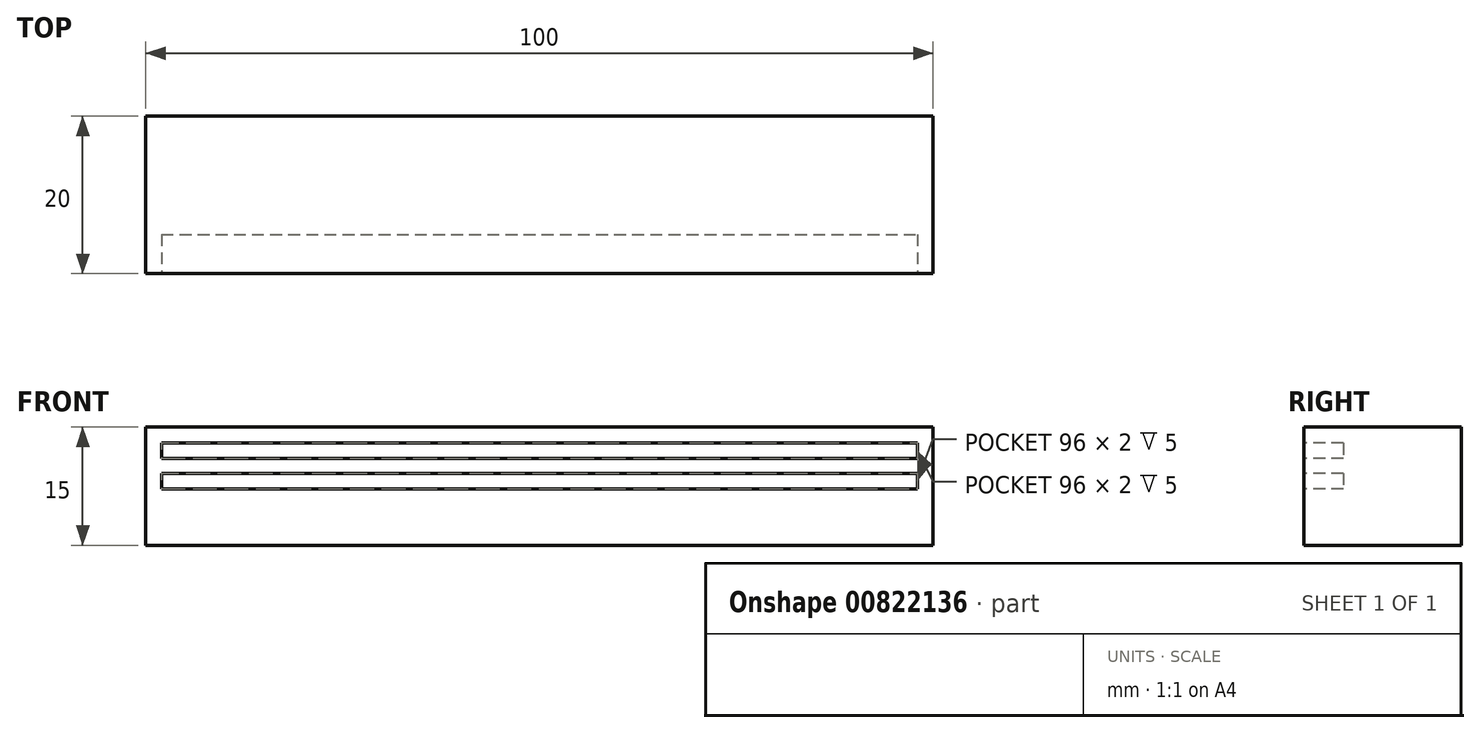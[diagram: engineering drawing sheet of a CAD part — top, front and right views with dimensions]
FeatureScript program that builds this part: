
annotation { "Feature Type Name" : "Feature", "Feature Type Description" : "" }
export const myFeature = defineFeature(function(context is Context, id is Id, definition is map)
    precondition{}
    {
        {
            var Q0;
            Q0=qCreatedBy(makeId("Front.planeOp"),FACE);
            var sketch = newSketch(context, id + "F0", { "sketchPlane" : qUnion([Q0])});
            skLineSegment(sketch, "E0.bottom", {"start": v(-50, 7.5) * mm, "end": v(50, 7.5) * mm});
            skLineSegment(sketch, "E0.top", {"start": v(-50, -7.5) * mm, "end": v(50, -7.5) * mm});
            skLineSegment(sketch, "E0.left", {"start": v(-50, 7.5) * mm, "end": v(-50, -7.5) * mm});
            skLineSegment(sketch, "E0.right", {"start": v(50, 7.5) * mm, "end": v(50, -7.5) * mm});
            skPoint(sketch, "E0.middle", {"position": v(0, 0) * mm});
            skSolve(sketch);
        }
        {
            var Q0;
            Q0=makeQuery(id+"F0.imprint","IMPRINT",FACE,{"disambiguationData":[TD([[makeQuery(id+"F0.imprint","IMPRINT",EDGE,{"derivedFrom":sQuery(id+"F0.wireOp",EDGE,"E0.bottom")}),-1.0]])]});
            extrude(context, id + "F1", {"entities" : qUnion([Q0]), "depth" : 20 * mm, "offsetDistance" : 25 * mm});
        }
        {
            var Q0;
            Q0=makeQuery(id+"F1.opExtrude","CAP_FACE",FACE,{"disambiguationData":[OSD([sQuery(id+"F0.wireOp",EDGE,"E0.bottom"),sQuery(id+"F0.wireOp",EDGE,"E0.top"),sQuery(id+"F0.wireOp",EDGE,"E0.left"),sQuery(id+"F0.wireOp",EDGE,"E0.right")])],"isStart":false});
            var sketch = newSketch(context, id + "F2", { "sketchPlane" : qUnion([Q0])});
            skLineSegment(sketch, "E1.bottom", {"start": v(-48, 5.5) * mm, "end": v(48, 5.5) * mm});
            skLineSegment(sketch, "E1.top", {"start": v(-48, 3.5) * mm, "end": v(48, 3.5) * mm});
            skLineSegment(sketch, "E1.left", {"start": v(-48, 5.5) * mm, "end": v(-48, 3.5) * mm});
            skLineSegment(sketch, "E1.right", {"start": v(48, 5.5) * mm, "end": v(48, 3.5) * mm});
            skPoint(sketch, "E1.middle", {"position": v(0, 4.5) * mm});
            skLineSegment(sketch, "E2.bottom", {"start": v(-48, 1.64) * mm, "end": v(48, 1.64) * mm});
            skLineSegment(sketch, "E2.top", {"start": v(-48, -0.36) * mm, "end": v(48, -0.36) * mm});
            skLineSegment(sketch, "E2.left", {"start": v(-48, 1.64) * mm, "end": v(-48, -0.36) * mm});
            skLineSegment(sketch, "E2.right", {"start": v(48, 1.64) * mm, "end": v(48, -0.36) * mm});
            skPoint(sketch, "E2.middle", {"position": v(0, 0.64) * mm});
            skSolve(sketch);
        }
        {
            var Q0;
            Q0 = qSketchRegion(id + "F2", true);
            extrude(context, id + "F3", {"entities" : qUnion([Q0]), "operationType" : NewBodyOperationType.REMOVE, "oppositeDirection" : true, "depth" : 5 * mm, "offsetDistance" : 25 * mm});
        }
    });
